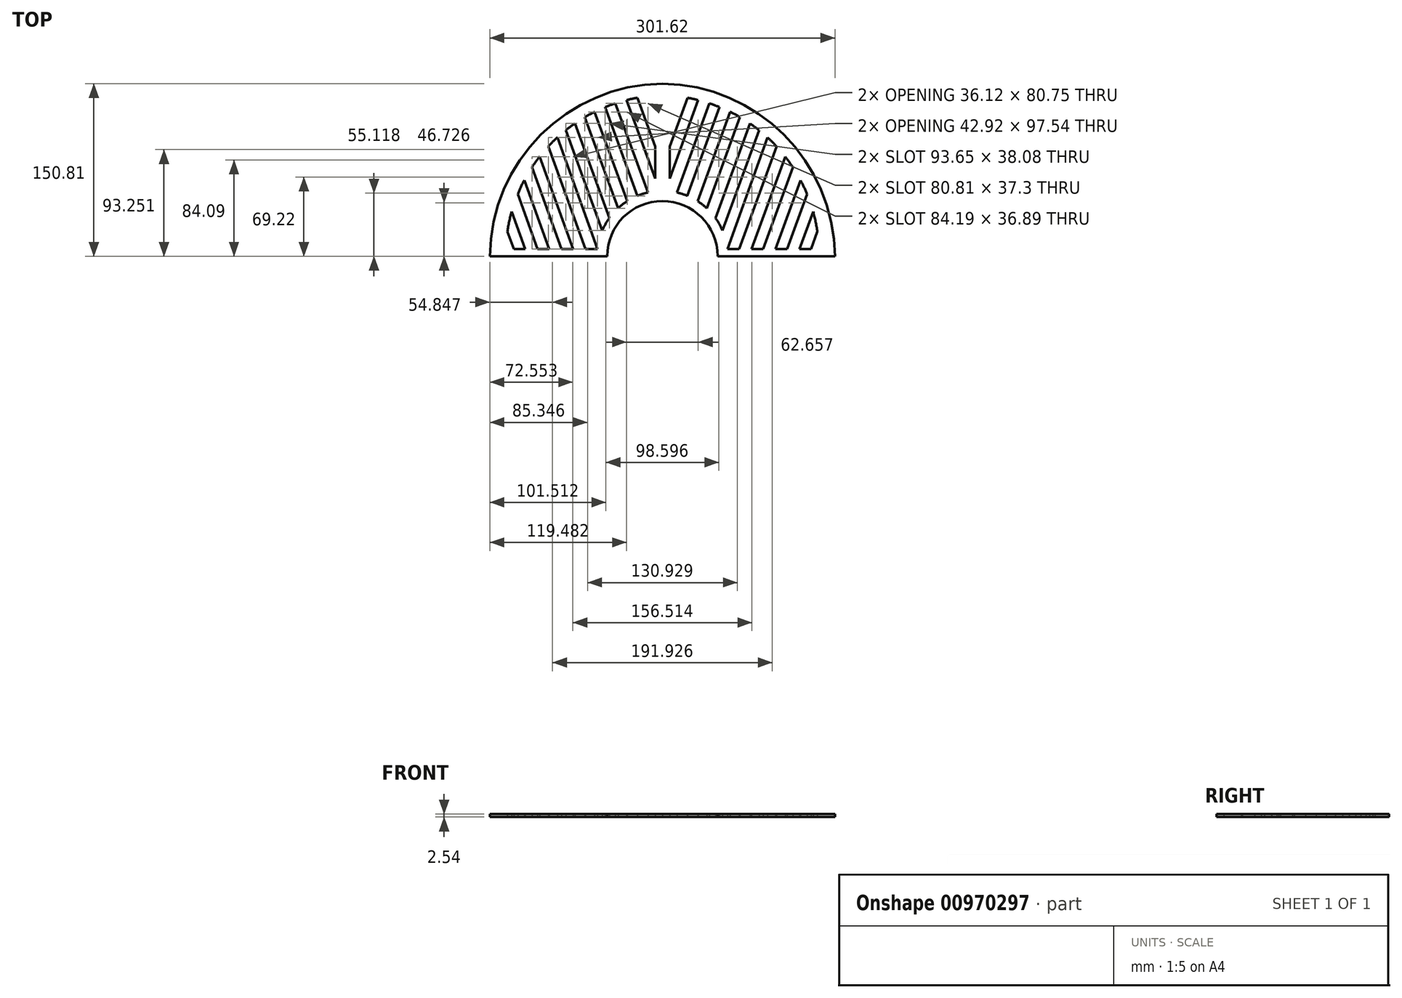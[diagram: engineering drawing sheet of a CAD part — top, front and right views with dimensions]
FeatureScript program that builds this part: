
annotation { "Feature Type Name" : "Feature", "Feature Type Description" : "" }
export const myFeature = defineFeature(function(context is Context, id is Id, definition is map)
    precondition{}
    {
        {
            var Q0;
            Q0=qCreatedBy(makeId("Top.planeOp"),FACE);
            var sketch = newSketch(context, id + "F0", { "sketchPlane" : qUnion([Q0])});
            skLineSegment(sketch, "E0", {"start": v(6.35, 68.05) * mm, "end": v(6.35, 95.9) * mm});
            skLineSegment(sketch, "E1", {"start": v(56.8, 6.35) * mm, "end": v(67.1, 6.35) * mm});
            skArc(sketch, "E2", {"start": v(52.58, 22.4) * mm, "mid": v(49.8, 28.03) * mm, "end": v(46.42, 33.33) * mm});
            skArc(sketch, "E3", {"start": v(135.47, 21.56) * mm, "mid": v(133.87, 30.37) * mm, "end": v(131.7, 39.06) * mm});
            skPoint(sketch, "E4.visualSharp", {"position": v(6.35, 140.4) * mm});
            skPoint(sketch, "E5.visualSharp", {"position": v(136.9, 6.35) * mm});
            skPoint(sketch, "E6.visualSharp", {"position": v(56.8, 6.35) * mm});
            skPoint(sketch, "E7.visualSharp", {"position": v(6.35, 56.8) * mm});
            skPoint(sketch, "E8", {"position": v(6.35, 62.22) * mm});
            skLineSegment(sketch, "E9", {"start": v(0, 0) * mm, "end": v(150.81, 0) * mm});
            skLineSegment(sketch, "E10", {"start": v(0, 0) * mm, "end": v(0, 150.81) * mm});
            skArc(sketch, "E11", {"start": v(150.81, 0) * mm, "mid": v(106.18, 106.18) * mm, "end": v(0, 150.81) * mm});
            skLineSegment(sketch, "E12", {"start": v(0, 150.81) * mm, "end": v(0, 150.81) * mm});
            skLineSegment(sketch, "E13", {"start": v(150.81, 0) * mm, "end": v(150.81, 0) * mm});
            skArc(sketch, "E14", {"start": v(0, 48.26) * mm, "mid": v(34.12, 34.12) * mm, "end": v(48.26, 0) * mm});
            skLineSegment(sketch, "E15", {"start": v(0, 0) * mm, "end": v(11.34, 31.17) * mm});
            skLineSegment(sketch, "E16", {"start": v(12.68, 55.73) * mm, "end": v(41.04, 133.66) * mm});
            skLineSegment(sketch, "E17", {"start": v(21.76, 52.84) * mm, "end": v(49.98, 130.37) * mm});
            skArc(sketch, "E18.trimOffspring", {"start": v(31.26, 136.5) * mm, "mid": v(26.58, 137.58) * mm, "end": v(21.86, 138.5) * mm});
            skLineSegment(sketch, "E19.trimOffspring", {"start": v(6.35, 68.05) * mm, "end": v(31.26, 136.5) * mm});
            skLineSegment(sketch, "E20", {"start": v(6.35, 95.9) * mm, "end": v(21.86, 138.5) * mm});
            skPoint(sketch, "E20.endSnap0", {"position": v(22.27, 138.43) * mm});
            skLineSegment(sketch, "E21", {"start": v(30.85, 48.1) * mm, "end": v(59.27, 126.19) * mm});
            skLineSegment(sketch, "E22", {"start": v(38.76, 42) * mm, "end": v(67.74, 121.62) * mm});
            skLineSegment(sketch, "E23", {"start": v(46.42, 33.33) * mm, "end": v(76.53, 116.04) * mm});
            skArc(sketch, "E24.trimOffspring", {"start": v(21.76, 52.84) * mm, "mid": v(17.28, 54.47) * mm, "end": v(12.68, 55.73) * mm});
            skArc(sketch, "E25.trimOffspring", {"start": v(38.76, 42) * mm, "mid": v(34.94, 45.22) * mm, "end": v(30.85, 48.1) * mm});
            skArc(sketch, "E26.trimOffspring", {"start": v(67.74, 121.62) * mm, "mid": v(63.55, 123.98) * mm, "end": v(59.27, 126.19) * mm});
            skArc(sketch, "E27.trimOffspring", {"start": v(49.98, 130.37) * mm, "mid": v(45.54, 132.09) * mm, "end": v(41.04, 133.66) * mm});
            skPoint(sketch, "E28.orphan", {"position": v(22.27, 139.65) * mm});
            skLineSegment(sketch, "E29", {"start": v(84.5, 110.12) * mm, "end": v(52.58, 22.4) * mm});
            skArc(sketch, "E30.trimOffspring", {"start": v(84.5, 110.12) * mm, "mid": v(80.57, 113.15) * mm, "end": v(76.53, 116.04) * mm});
            skLineSegment(sketch, "E31.trimOffspring", {"start": v(56.8, 6.35) * mm, "end": v(91.78, 103.89) * mm});
            skLineSegment(sketch, "E32", {"start": v(67.1, 6.35) * mm, "end": v(99.72, 95.99) * mm});
            skLineSegment(sketch, "E33", {"start": v(77.9, 6.35) * mm, "end": v(107.3, 87.1) * mm});
            skLineSegment(sketch, "E34", {"start": v(88.04, 6.35) * mm, "end": v(114.02, 77.74) * mm});
            skLineSegment(sketch, "E35", {"start": v(98.85, 6.35) * mm, "end": v(120.72, 66.43) * mm});
            skLineSegment(sketch, "E36.trimOffspring", {"start": v(77.9, 6.35) * mm, "end": v(88.04, 6.35) * mm});
            skLineSegment(sketch, "E37.trimOffspring", {"start": v(98.85, 6.35) * mm, "end": v(108.99, 6.35) * mm});
            skArc(sketch, "E38.trimOffspring", {"start": v(114.02, 77.74) * mm, "mid": v(110.76, 82.49) * mm, "end": v(107.3, 87.1) * mm});
            skArc(sketch, "E39.trimOffspring", {"start": v(99.72, 95.99) * mm, "mid": v(95.83, 100.02) * mm, "end": v(91.78, 103.89) * mm});
            skLineSegment(sketch, "E40", {"start": v(108.99, 6.35) * mm, "end": v(126.43, 54.27) * mm});
            skLineSegment(sketch, "E41", {"start": v(119.8, 6.35) * mm, "end": v(131.7, 39.06) * mm});
            skLineSegment(sketch, "E42", {"start": v(129.94, 6.35) * mm, "end": v(135.47, 21.56) * mm});
            skLineSegment(sketch, "E43.trimOffspring", {"start": v(119.8, 6.35) * mm, "end": v(130.7, 6.35) * mm});
            skArc(sketch, "E44.trimOffspring", {"start": v(126.43, 54.27) * mm, "mid": v(123.72, 60.42) * mm, "end": v(120.72, 66.43) * mm});
            skPoint(sketch, "E45.trimOffspring.end.orphan", {"position": v(13.3, 139.65) * mm});
            skSolve(sketch);
        }
        {
            var Q0;
            Q0=makeQuery(id+"F0.imprint","IMPRINT",FACE,{"disambiguationData":[TD([[makeQuery(id+"F0.imprint","IMPRINT",EDGE,{"derivedFrom":sQuery(id+"F0.wireOp",EDGE,"E0")}),1.0]])]});
            extrude(context, id + "F1", {"entities" : qUnion([Q0]), "depth" : 2.54 * mm, "offsetDistance" : 25.4 * mm});
        }
        {
            var Q0;
            Q0=makeQuery(id+"F1.opExtrude","SWEPT_BODY",BODY,{"disambiguationData":[OSD([sQuery(id+"F0.wireOp",EDGE,"E0"),sQuery(id+"F0.wireOp",EDGE,"E1"),sQuery(id+"F0.wireOp",EDGE,"E2"),sQuery(id+"F0.wireOp",EDGE,"E3"),sQuery(id+"F0.wireOp",EDGE,"E9"),sQuery(id+"F0.wireOp",EDGE,"E10"),sQuery(id+"F0.wireOp",EDGE,"E11"),sQuery(id+"F0.wireOp",EDGE,"E14"),sQuery(id+"F0.wireOp",EDGE,"E16"),sQuery(id+"F0.wireOp",EDGE,"E17"),sQuery(id+"F0.wireOp",EDGE,"E18.trimOffspring"),sQuery(id+"F0.wireOp",EDGE,"E19.trimOffspring"),sQuery(id+"F0.wireOp",EDGE,"E20"),sQuery(id+"F0.wireOp",EDGE,"E21"),sQuery(id+"F0.wireOp",EDGE,"E22"),sQuery(id+"F0.wireOp",EDGE,"E23"),sQuery(id+"F0.wireOp",EDGE,"E24.trimOffspring"),sQuery(id+"F0.wireOp",EDGE,"E25.trimOffspring"),sQuery(id+"F0.wireOp",EDGE,"E26.trimOffspring"),sQuery(id+"F0.wireOp",EDGE,"E27.trimOffspring"),sQuery(id+"F0.wireOp",EDGE,"E29"),sQuery(id+"F0.wireOp",EDGE,"E30.trimOffspring"),sQuery(id+"F0.wireOp",EDGE,"E31.trimOffspring"),sQuery(id+"F0.wireOp",EDGE,"E32"),sQuery(id+"F0.wireOp",EDGE,"E33"),sQuery(id+"F0.wireOp",EDGE,"E34"),sQuery(id+"F0.wireOp",EDGE,"E35"),sQuery(id+"F0.wireOp",EDGE,"E36.trimOffspring"),sQuery(id+"F0.wireOp",EDGE,"E37.trimOffspring"),sQuery(id+"F0.wireOp",EDGE,"E38.trimOffspring"),sQuery(id+"F0.wireOp",EDGE,"E39.trimOffspring"),sQuery(id+"F0.wireOp",EDGE,"E40"),sQuery(id+"F0.wireOp",EDGE,"E41"),sQuery(id+"F0.wireOp",EDGE,"E42"),sQuery(id+"F0.wireOp",EDGE,"E43.trimOffspring"),sQuery(id+"F0.wireOp",EDGE,"E44.trimOffspring")])]});
            var Q1;
            Q1=qCreatedBy(makeId("Right.planeOp"),FACE);
            mirror(context, id + "F2", {"operationType" : NewBodyOperationType.ADD, "entities" : qUnion([Q0]), "mirrorPlane" : qUnion([Q1])});
        }
    });
